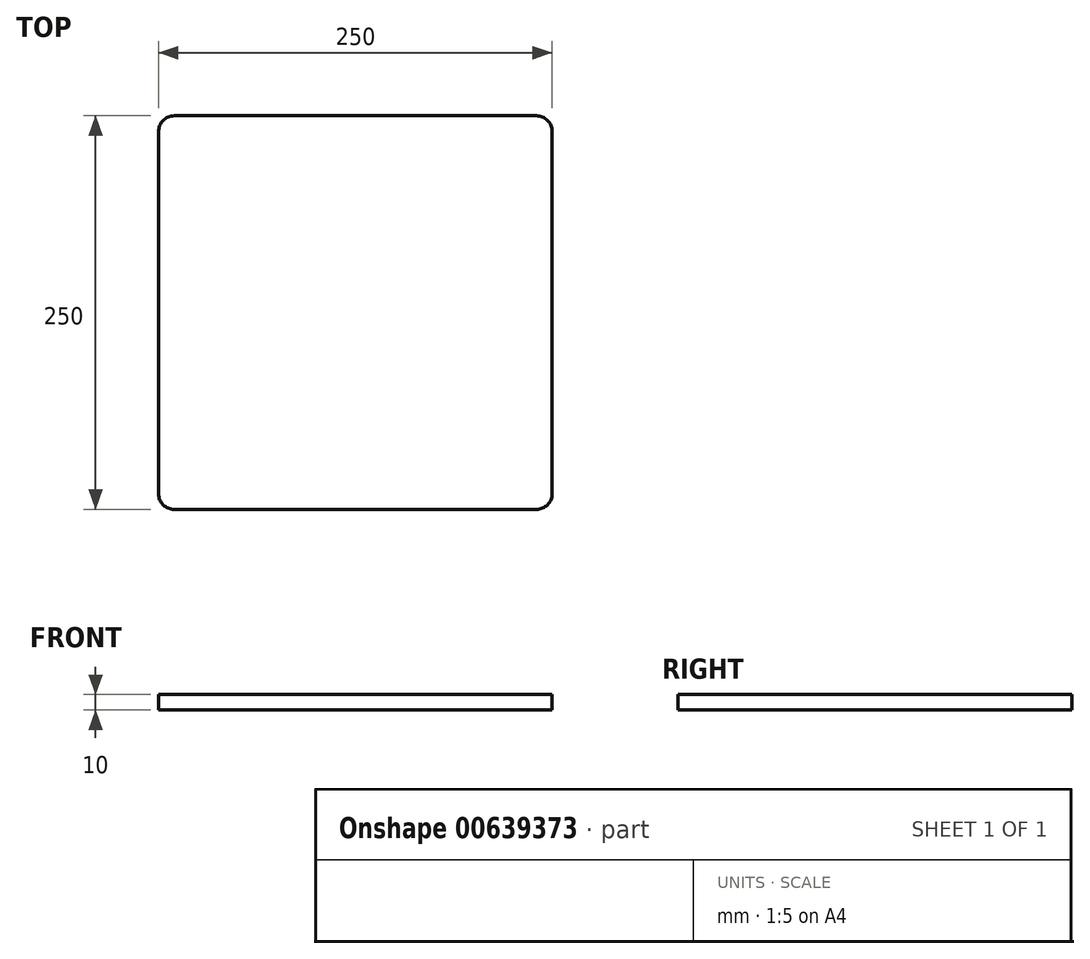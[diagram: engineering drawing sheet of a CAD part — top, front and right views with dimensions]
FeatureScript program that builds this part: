
annotation { "Feature Type Name" : "Feature", "Feature Type Description" : "" }
export const myFeature = defineFeature(function(context is Context, id is Id, definition is map)
    precondition{}
    {
        {
            var Q0;
            Q0=qCreatedBy(makeId("Top.planeOp"),FACE);
            var sketch = newSketch(context, id + "F0", { "sketchPlane" : qUnion([Q0])});
            skLineSegment(sketch, "E0.bottom", {"start": v(-202.04, 219.09) * mm, "end": v(47.96, 219.09) * mm});
            skLineSegment(sketch, "E0.top", {"start": v(-202.04, -30.91) * mm, "end": v(47.96, -30.91) * mm});
            skLineSegment(sketch, "E0.left", {"start": v(-202.04, 219.09) * mm, "end": v(-202.04, -30.91) * mm});
            skLineSegment(sketch, "E0.right", {"start": v(47.96, 219.09) * mm, "end": v(47.96, -30.91) * mm});
            skSolve(sketch);
        }
        {
            var Q0;
            Q0=makeQuery(id+"F0.imprint","IMPRINT",FACE,{"disambiguationData":[TD([[makeQuery(id+"F0.imprint","IMPRINT",EDGE,{"derivedFrom":sQuery(id+"F0.wireOp",EDGE,"E0.bottom")}),-1.0]])]});
            extrude(context, id + "F1", {"entities" : qUnion([Q0]), "depth" : 10 * mm, "offsetDistance" : 25 * mm});
        }
        {
            var Q0;
            Q0=makeQuery(id+"F1.opExtrude","SWEPT_EDGE",EDGE,{"disambiguationData":[OSD([sQuery(id+"F0.wireOp",EDGE,"E0.top"),sQuery(id+"F0.wireOp",EDGE,"E0.right")])]});
            var Q1;
            Q1=makeQuery(id+"F1.opExtrude","SWEPT_EDGE",EDGE,{"disambiguationData":[OSD([sQuery(id+"F0.wireOp",EDGE,"E0.top"),sQuery(id+"F0.wireOp",EDGE,"E0.left")])]});
            var Q2;
            Q2=makeQuery(id+"F1.opExtrude","SWEPT_EDGE",EDGE,{"disambiguationData":[OSD([sQuery(id+"F0.wireOp",EDGE,"E0.bottom"),sQuery(id+"F0.wireOp",EDGE,"E0.right")])]});
            var Q3;
            Q3=makeQuery(id+"F1.opExtrude","SWEPT_EDGE",EDGE,{"disambiguationData":[OSD([sQuery(id+"F0.wireOp",EDGE,"E0.bottom"),sQuery(id+"F0.wireOp",EDGE,"E0.left")])]});
            fillet(context, id + "F2", {"entities" : qUnion([Q0, Q1, Q2, Q3]), "radius" : 10 * mm, "tangentPropagation" : true, "allowEdgeOverflow" : false});
        }
    });
